# Revit family: QF_VOLLRATH_38203_SERVEWELL_SL_HOT_FOOD_TABLE
name_source: partatom
category: Specialty Equipment
units: mm (PartAtom-declared; Revit-internal decimal feet)

## family parameters
Always vertical = Yes
Cut with Voids When Loaded = No
Maintain Annotation Orientation = No
Part Type = Normal
Room Calculation Point = No
Round Connector Dimension = Use Diameter
Shared = No
Work Plane-Based = No

## types (1)
- QF_VOLLRATH_38203_SERVEWELL_SL_HOT_FOOD_TABLE
    Apparent Power = 1800 VA
    Conn Conduit = Yes
    Conn Plug = NEMA 5-15P
    Cycle = 0 Hz
    Default Elevation = 0"
    Depth = 29 1/2"
    Description = SERVEWELL SL HOT FOOD TABLE
    Elec Conn Connection Height = 0"
    Elec Conn RI Height = 0"
    FL Amps = 15 A
    Foodservice Equipment Identifier = Yes
    Height = 34"
    Identify Quantity as Lot = Yes
    Length = 46"
    Manufacturer = VOLLRATH
    Max Overcurrent Protection = 0 A
    Min Ckt Ampacity = 0 A
    Model = 38203
    Number of Poles = 1
    Phase = 1
    Volts = 120 V
    Watts = 1440 W
    Weight in Pounds = 0

## geometry (parser evidence)
native form markers: Sweep x7
no freeform markers — native parametric forms only
